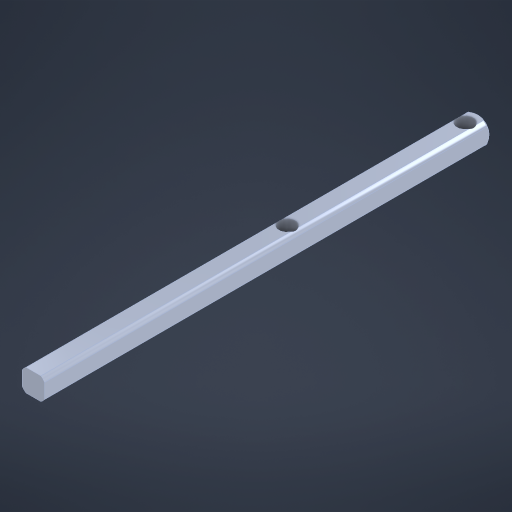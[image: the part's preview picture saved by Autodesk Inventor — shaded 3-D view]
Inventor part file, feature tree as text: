
AUTODESK INVENTOR PART (.ipt)
format: ipt  version: 2024 (Build 280153000, 153)  size: 311,808 bytes
history: native  units: in
note: dims shown in document units (in); Inventor stores cm internally (conversion verified against a paired STEP export)
features: other x50, sketch x3, extrude x2, thicken_offset x1, hole x1
ambient origin geometry x8: Origin, YZ Plane, XZ Plane, XY Plane, X Axis, Y Axis, Z Axis, Center Point
bodies: Solid1 (feature_tree)
feature tree (57):
  other  "Table"
  other  "Shaft HS 0.5 in"
  other  "Shaft HS 1.0 in"
  other  "Shaft HS 1.5 in"
  other  "Shaft HS 2.0 in"
  other  "Shaft HS 2.5 in"
  other  "Shaft HS 3.0 in"
  other  "Shaft HS 3.5 in"
  other  "Shaft HS 4.0 in"
  other  "Shaft HS 4.5 in"
  other  "Shaft HS 5.0 in"
  other  "Shaft HS 5.5 in"
  other  "Shaft HS 6.0 in"
  other  "Shaft HS 6.5 in"
  other  "Shaft HS 7.0 in"
  other  "Shaft HS 7.5 in"
  other  "Shaft HS 8.0 in"
  other  "Shaft HS 8.5 in"
  other  "Shaft HS 9.0 in"
  other  "Shaft HS 9.5 in"
  other  "Shaft HS 10.0 in"
  other  "Shaft HS 10.5 in"
  other  "Shaft HS 11.0 in"
  other  "Shaft HS 11.5 in"
  other  "Shaft HS 12.0 in"
  other  "Shaft HS 12.5 in"
  other  "Shaft HS 13.0 in"
  other  "Shaft HS 13.5 in"
  other  "Shaft HS 14.0 in"
  other  "Shaft HS 14.5 in"
  other  "Shaft HS 15.0 in"
  other  "Shaft HS 15.5 in"
  other  "Shaft HS 16.0 in"
  other  "Shaft HS 16.5 in"
  other  "Shaft HS 17.0 in"
  other  "Shaft HS 17.5 in"
  other  "Shaft HS 18.0 in"
  other  "Shaft HS 18.5 in"
  other  "Shaft HS 19.0 in"
  other  "Shaft HS 19.5 in"
  other  "Shaft HS 20.0 in"
  other  "Shaft HS 20.5 in"
  other  "Shaft HS 21.0 in"
  other  "Shaft HS 21.5 in"
  other  "Shaft HS 22.0 in"
  other  "Shaft HS 22.5 in"
  other  "Shaft HS 23.0 in"
  other  "Shaft HS 23.5 in"
  other  "Shaft HS 24.0 in"
  other  "Cut-Revolve3"
  extrude  "Extrusion1"  Depth=12.1875in
  thicken_offset  "Thicken1"
  extrude  "Extrusion2"  Depth=19.125in
  hole  "Hole1"  [1 undecoded]
  sketch  "Sketch2"  dims[d0=0.0625in d1=0.0in d2=12.1875in]
  sketch  "Sketch3"  dims[d3=12.125in d4=19.125in]
  sketch  "Sketch6"  dims[d5=0.0in d9=0.15in d11=0.1875in d12=0.75in d13=0.375in d14=0.25in d15=0.5635in d16=1.0in d17=0.8108in d18=2.0in]
note: 1 required parameter value undecoded (feature->parameter linkage not recoverable at this tier; creation-order binding heuristic only, values carry confidence <= 0.55)
